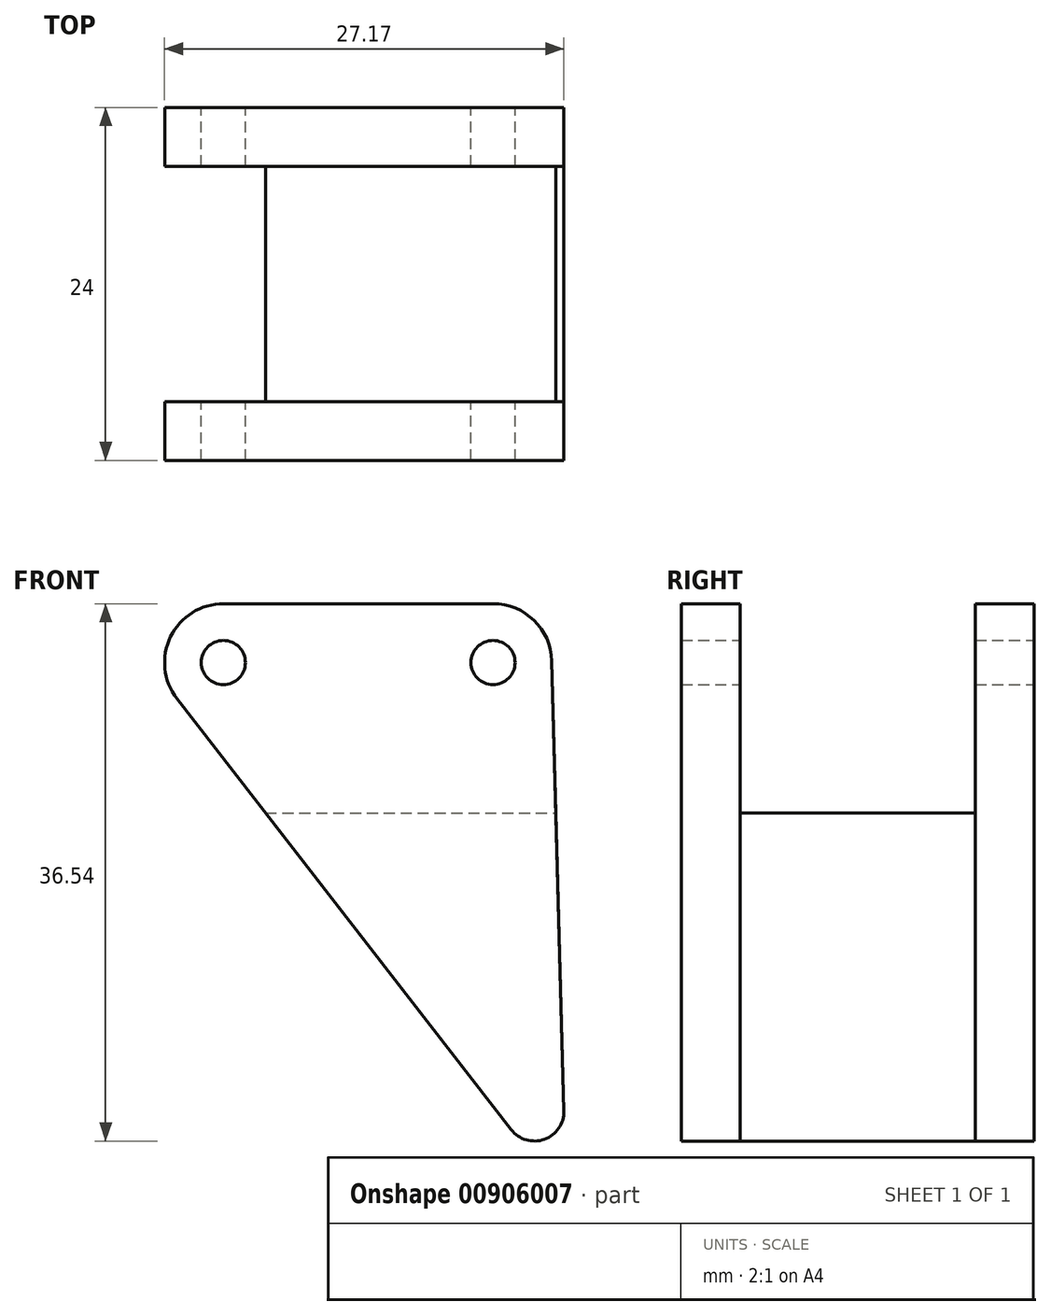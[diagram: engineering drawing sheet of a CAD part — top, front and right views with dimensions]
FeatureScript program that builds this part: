
annotation { "Feature Type Name" : "Feature", "Feature Type Description" : "" }
export const myFeature = defineFeature(function(context is Context, id is Id, definition is map)
    precondition{}
    {
        {
            var Q0;
            Q0=qCreatedBy(makeId("Front.planeOp"),FACE);
            var sketch = newSketch(context, id + "F0", { "sketchPlane" : qUnion([Q0])});
            skLineSegment(sketch, "E0", {"start": v(-24.33, 28.09) * mm, "end": v(-1.58, -1.23) * mm});
            skLineSegment(sketch, "E1", {"start": v(2, 0.05) * mm, "end": v(1.18, 30.65) * mm});
            skLineSegment(sketch, "E2", {"start": v(-2.82, 34.54) * mm, "end": v(-21.17, 34.54) * mm});
            skPoint(sketch, "E3.visualSharp", {"position": v(-29.33, 34.54) * mm});
            skArc(sketch, "E3.filletArc", {"start": v(-21.17, 34.54) * mm, "mid": v(-24.76, 32.3) * mm, "end": v(-24.33, 28.09) * mm});
            skPoint(sketch, "E4.visualSharp", {"position": v(1.08, 34.54) * mm});
            skArc(sketch, "E4.filletArc", {"start": v(1.18, 30.65) * mm, "mid": v(-0.03, 33.4) * mm, "end": v(-2.82, 34.54) * mm});
            skPoint(sketch, "E5.visualSharp", {"position": v(2.16, -6.05) * mm});
            skArc(sketch, "E5.filletArc", {"start": v(-1.58, -1.23) * mm, "mid": v(0.67, -1.88) * mm, "end": v(2, 0.05) * mm});
            skCircle(sketch, "E6", {"center": v(-2.82, 30.54) * mm, "radius": 1.5 * mm});
            skCircle(sketch, "E7", {"center": v(-21.17, 30.54) * mm, "radius": 1.5 * mm});
            skSolve(sketch);
        }
        {
            var Q0;
            Q0=qSketchRegion(id+"F0",true);
            extrude(context, id + "F1", {"entities" : qUnion([Q0]), "endBound" : BoundingType.SYMMETRIC, "depth" : 24 * mm, "offsetDistance" : 25.4 * mm});
        }
        {
            var Q0;
            Q0=qCreatedBy(makeId("Front.planeOp"),FACE);
            var sketch = newSketch(context, id + "F2", { "sketchPlane" : qUnion([Q0])});
            skLineSegment(sketch, "E8.0.0", {"start": v(2, 0.05) * mm, "end": v(1.18, 30.65) * mm});
            skArc(sketch, "E8.0.1", {"start": v(1.18, 30.65) * mm, "mid": v(-0.03, 33.4) * mm, "end": v(-2.82, 34.54) * mm});
            skLineSegment(sketch, "E8.0.2", {"start": v(-2.82, 34.54) * mm, "end": v(-21.17, 34.54) * mm});
            skArc(sketch, "E8.0.3", {"start": v(-21.17, 34.54) * mm, "mid": v(-24.76, 32.3) * mm, "end": v(-24.33, 28.09) * mm});
            skLineSegment(sketch, "E8.0.4", {"start": v(-24.33, 28.09) * mm, "end": v(-1.58, -1.23) * mm});
            skArc(sketch, "E8.0.5", {"start": v(-1.58, -1.23) * mm, "mid": v(0.67, -1.88) * mm, "end": v(2, 0.05) * mm});
            skSolve(sketch);
        }
        {
            var Q0;
            Q0=qSketchRegion(id+"F2",true);
            extrude(context, id + "F3", {"entities" : qUnion([Q0]), "operationType" : NewBodyOperationType.REMOVE, "endBound" : BoundingType.SYMMETRIC, "oppositeDirection" : true, "depth" : 16 * mm, "offsetDistance" : 25.4 * mm});
        }
        {
            var Q0;
            Q0=makeQuery(id+"F3.boolean.opBoolean","COPY",FACE,{"derivedFrom":makeQuery(id+"F3.opExtrude","CAP_FACE",FACE,{"disambiguationData":[OSD([sQuery(id+"F2.wireOp",EDGE,"E8.0.0"),sQuery(id+"F2.wireOp",EDGE,"E8.0.1"),sQuery(id+"F2.wireOp",EDGE,"E8.0.2"),sQuery(id+"F2.wireOp",EDGE,"E8.0.3"),sQuery(id+"F2.wireOp",EDGE,"E8.0.4"),sQuery(id+"F2.wireOp",EDGE,"E8.0.5")])],"isStart":false})});
            var sketch = newSketch(context, id + "F4", { "sketchPlane" : qUnion([Q0])});
            skLineSegment(sketch, "E9.0.0", {"start": v(2, 0.05) * mm, "end": v(1.18, 30.65) * mm});
            skArc(sketch, "E9.0.1", {"start": v(1.18, 30.65) * mm, "mid": v(-0.03, 33.4) * mm, "end": v(-2.82, 34.54) * mm});
            skArc(sketch, "E9.0.3", {"start": v(-21.17, 34.54) * mm, "mid": v(-24.76, 32.3) * mm, "end": v(-24.33, 28.09) * mm});
            skLineSegment(sketch, "E9.0.4", {"start": v(-24.33, 28.09) * mm, "end": v(-1.58, -1.23) * mm});
            skArc(sketch, "E9.0.5", {"start": v(-1.58, -1.23) * mm, "mid": v(0.67, -1.88) * mm, "end": v(2, 0.05) * mm});
            skLineSegment(sketch, "E10", {"start": v(-18.3, 20.32) * mm, "end": v(1.46, 20.32) * mm});
            skSolve(sketch);
        }
        {
            var Q0;
            Q0=qSketchRegion(id+"F4",true);
            extrude(context, id + "F5", {"entities" : qUnion([Q0]), "depth" : 16 * mm, "offsetDistance" : 25.4 * mm});
        }
    });
